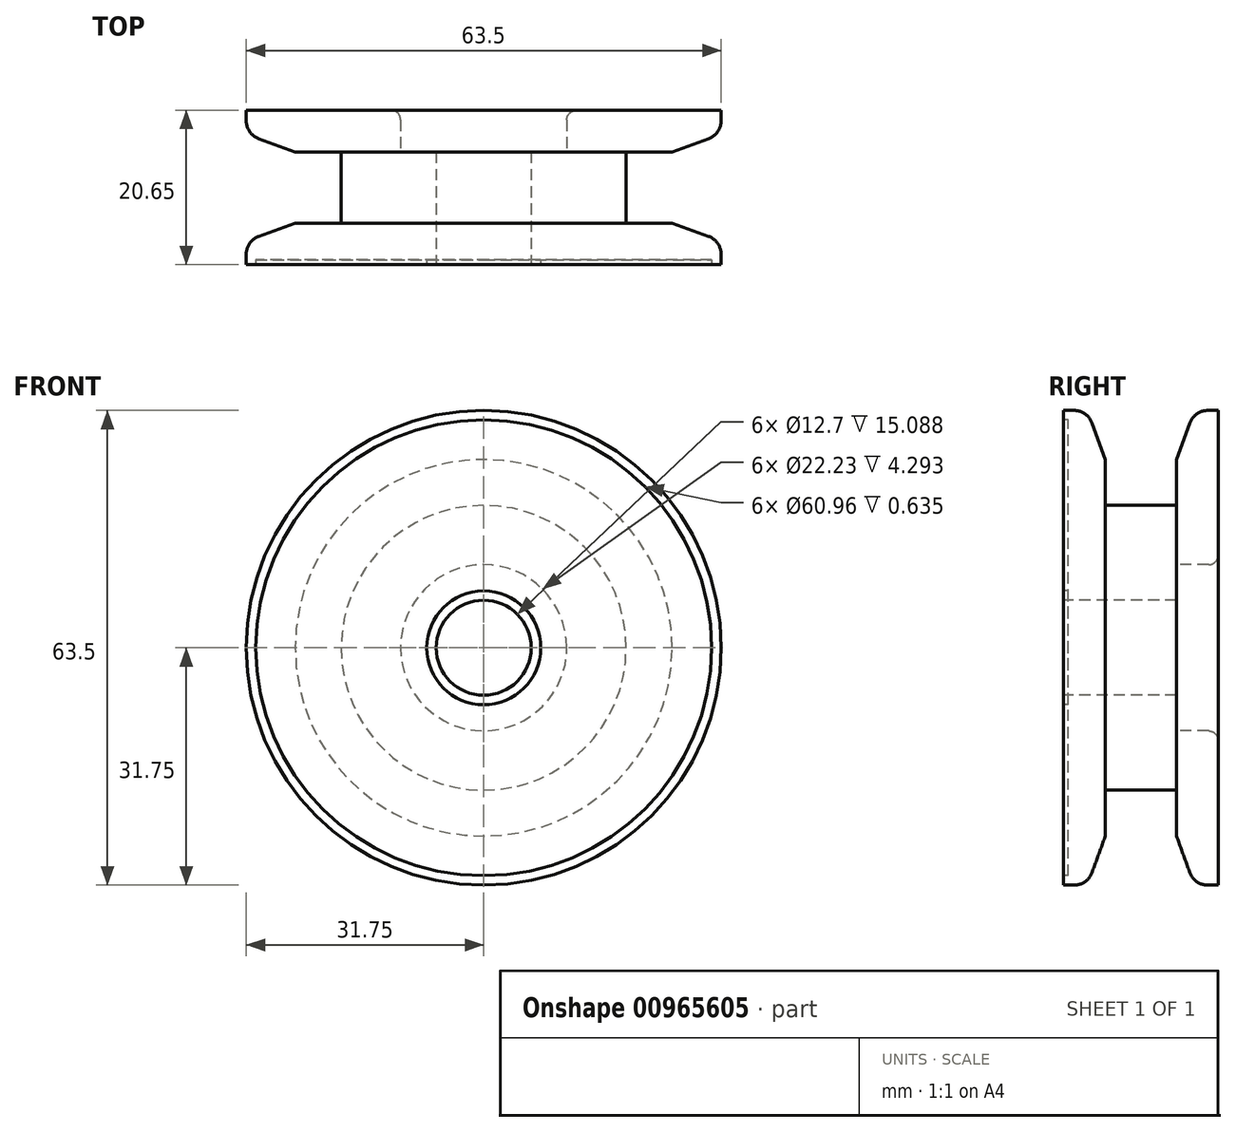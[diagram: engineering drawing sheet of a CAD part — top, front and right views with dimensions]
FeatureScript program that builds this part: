
annotation { "Feature Type Name" : "Feature", "Feature Type Description" : "" }
export const myFeature = defineFeature(function(context is Context, id is Id, definition is map)
    precondition{}
    {
        {
            var Q0;
            Q0=qCreatedBy(makeId("Right.planeOp"),FACE);
            var sketch = newSketch(context, id + "F0", { "sketchPlane" : qUnion([Q0])});
            skLineSegment(sketch, "E0", {"start": v(-7.4, 0) * mm, "end": v(13.03, 0) * mm, "construction": true});
            skLineSegment(sketch, "E1", {"start": v(7.17, 6.35) * mm, "end": v(7.17, 11.11) * mm});
            skLineSegment(sketch, "E2", {"start": v(7.17, 11.11) * mm, "end": v(12.73, 11.11) * mm});
            skLineSegment(sketch, "E3", {"start": v(12.73, 11.11) * mm, "end": v(12.73, 31.75) * mm});
            skLineSegment(sketch, "E4", {"start": v(12.73, 31.75) * mm, "end": v(9.56, 31.75) * mm});
            skLineSegment(sketch, "E5", {"start": v(9.56, 31.75) * mm, "end": v(7.17, 25.2) * mm});
            skLineSegment(sketch, "E6", {"start": v(7.17, 25.2) * mm, "end": v(7.17, 19.05) * mm});
            skLineSegment(sketch, "E7", {"start": v(7.17, 19.05) * mm, "end": v(-2.35, 19.05) * mm});
            skLineSegment(sketch, "E8", {"start": v(-2.35, 19.05) * mm, "end": v(-2.35, 25.2) * mm});
            skLineSegment(sketch, "E9", {"start": v(-2.35, 25.2) * mm, "end": v(-4.74, 31.75) * mm});
            skLineSegment(sketch, "E10", {"start": v(-4.74, 31.75) * mm, "end": v(-7.92, 31.75) * mm});
            skLineSegment(sketch, "E11", {"start": v(-7.92, 6.35) * mm, "end": v(7.17, 6.35) * mm});
            skLineSegment(sketch, "E12", {"start": v(-7.92, 6.35) * mm, "end": v(-7.92, 7.62) * mm});
            skLineSegment(sketch, "E13", {"start": v(-7.92, 7.62) * mm, "end": v(-7.28, 7.62) * mm});
            skLineSegment(sketch, "E14", {"start": v(-7.28, 7.62) * mm, "end": v(-7.28, 30.48) * mm});
            skLineSegment(sketch, "E15", {"start": v(-7.28, 30.48) * mm, "end": v(-7.92, 30.48) * mm});
            skLineSegment(sketch, "E16.trimOffspring", {"start": v(-7.92, 30.48) * mm, "end": v(-7.92, 31.75) * mm});
            skSolve(sketch);
        }
        {
            var Q0;
            Q0=makeQuery(id+"F0.imprint","IMPRINT",FACE,{"disambiguationData":[TD([[makeQuery(id+"F0.imprint","IMPRINT",EDGE,{"derivedFrom":sQuery(id+"F0.wireOp",EDGE,"E1")}),1.0]])]});
            var Q1;
            Q1=sQuery(id+"F0.wireOp",EDGE,"E0");
            revolve(context, id + "F1", {"surfaceOperationType" : NewSurfaceOperationType.NEW, "entities" : qUnion([Q0]), "axis" : qUnion([Q1]), "revolveType" : RevolveType.FULL});
        }
        {
            var Q0;
            Q0=makeQuery(id+"F1.opRevolve","SWEPT_EDGE",EDGE,{"disambiguationData":[OSD([sQuery(id+"F0.wireOp",EDGE,"E4"),sQuery(id+"F0.wireOp",EDGE,"E5")])]});
            var Q1;
            Q1=makeQuery(id+"F1.opRevolve","SWEPT_EDGE",EDGE,{"disambiguationData":[OSD([sQuery(id+"F0.wireOp",EDGE,"E9"),sQuery(id+"F0.wireOp",EDGE,"E10")])]});
            fillet(context, id + "F2", {"entities" : qUnion([Q0, Q1]), "radius" : 2.54 * mm, "tangentPropagation" : true, "allowEdgeOverflow" : false});
        }
        {
            var Q0;
            Q0=makeQuery(id+"F1.opRevolve","SWEPT_EDGE",EDGE,{"disambiguationData":[OSD([sQuery(id+"F0.wireOp",EDGE,"E2"),sQuery(id+"F0.wireOp",EDGE,"E3")])]});
            fillet(context, id + "F3", {"entities" : qUnion([Q0]), "radius" : 1.27 * mm, "tangentPropagation" : true, "allowEdgeOverflow" : false});
        }
    });
